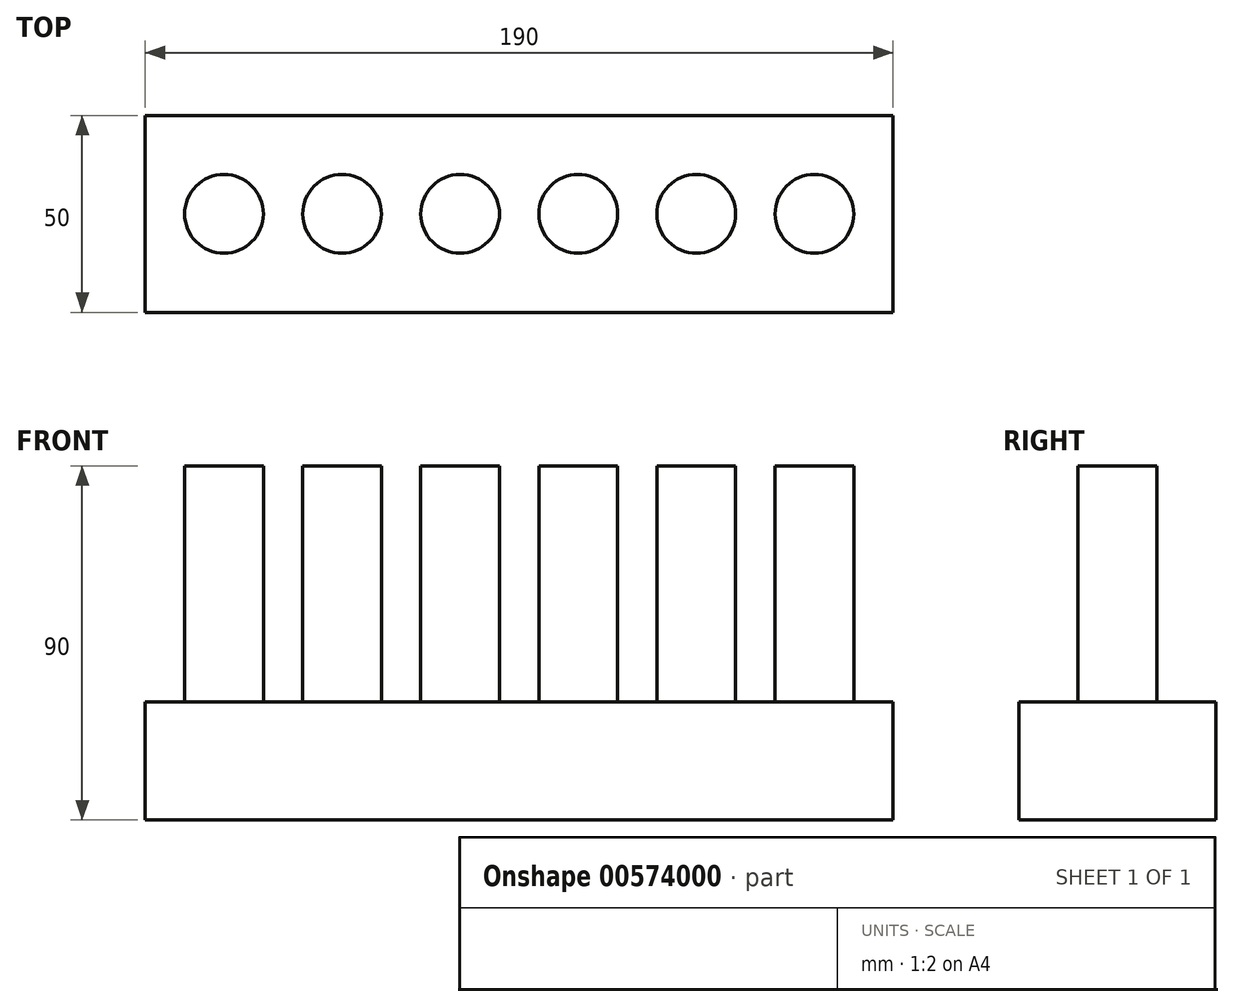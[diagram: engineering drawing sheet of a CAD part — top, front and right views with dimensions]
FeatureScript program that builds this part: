
annotation { "Feature Type Name" : "Feature", "Feature Type Description" : "" }
export const myFeature = defineFeature(function(context is Context, id is Id, definition is map)
    precondition{}
    {
        {
            var Q0;
            Q0=qCreatedBy(makeId("Top.planeOp"),FACE);
            var sketch = newSketch(context, id + "F0", { "sketchPlane" : qUnion([Q0])});
            skLineSegment(sketch, "E0.bottom", {"start": v(0, -25) * mm, "end": v(95, -25) * mm});
            skLineSegment(sketch, "E0.top", {"start": v(0, 25) * mm, "end": v(95, 25) * mm});
            skLineSegment(sketch, "E0.left", {"start": v(0, -25) * mm, "end": v(0, 25) * mm});
            skLineSegment(sketch, "E0.right", {"start": v(95, -25) * mm, "end": v(95, 25) * mm});
            skSolve(sketch);
        }
        {
            var Q0;
            Q0 = qSketchRegion(id + "F0", true);
            extrude(context, id + "F1", {"entities" : qUnion([Q0]), "depth" : 30 * mm, "offsetDistance" : 25 * mm});
        }
        {
            var Q0;
            Q0=makeQuery(id+"F1.opExtrude","CAP_FACE",FACE,{"disambiguationData":[OSD([sQuery(id+"F0.wireOp",EDGE,"E0.bottom"),sQuery(id+"F0.wireOp",EDGE,"E0.top"),sQuery(id+"F0.wireOp",EDGE,"E0.left"),sQuery(id+"F0.wireOp",EDGE,"E0.right")])],"isStart":false});
            var sketch = newSketch(context, id + "F2", { "sketchPlane" : qUnion([Q0])});
            skCircle(sketch, "E1", {"center": v(75, 0) * mm, "radius": 10 * mm});
            skCircle(sketch, "E2", {"center": v(15, 0) * mm, "radius": 10 * mm});
            skCircle(sketch, "E3", {"center": v(45, 0) * mm, "radius": 10 * mm});
            skSolve(sketch);
        }
        {
            var Q0;
            Q0 = qSketchRegion(id + "F2", true);
            extrude(context, id + "F3", {"entities" : qUnion([Q0]), "operationType" : NewBodyOperationType.REMOVE, "oppositeDirection" : true, "depth" : 10 * mm, "offsetDistance" : 25 * mm});
        }
        {
            var Q0;
            Q0=makeQuery(id+"F3.boolean.opBoolean","COPY",FACE,{"derivedFrom":makeQuery(id+"F3.opExtrude","CAP_FACE",FACE,{"disambiguationData":[OSD([sQuery(id+"F2.wireOp",EDGE,"E1")])],"isStart":false})});
            var sketch = newSketch(context, id + "F4", { "sketchPlane" : qUnion([Q0])});
            skCircle(sketch, "E4", {"center": v(75, 0) * mm, "radius": 10 * mm});
            skSolve(sketch);
        }
        {
            var Q0;
            Q0 = qSketchRegion(id + "F4", true);
            extrude(context, id + "F5", {"entities" : qUnion([Q0]), "operationType" : NewBodyOperationType.ADD, "depth" : 70 * mm, "offsetDistance" : 25 * mm});
        }
        {
            var Q0;
            Q0=makeQuery(id+"F3.boolean.opBoolean","COPY",FACE,{"derivedFrom":makeQuery(id+"F3.opExtrude","CAP_FACE",FACE,{"disambiguationData":[OSD([sQuery(id+"F2.wireOp",EDGE,"E3")])],"isStart":false})});
            var sketch = newSketch(context, id + "F6", { "sketchPlane" : qUnion([Q0])});
            skCircle(sketch, "E5", {"center": v(45, 0) * mm, "radius": 10 * mm});
            skSolve(sketch);
        }
        {
            var Q0;
            Q0 = qSketchRegion(id + "F6", true);
            extrude(context, id + "F7", {"entities" : qUnion([Q0]), "operationType" : NewBodyOperationType.ADD, "depth" : 70 * mm, "offsetDistance" : 25 * mm});
        }
        {
            var Q0;
            Q0=makeQuery(id+"F3.boolean.opBoolean","COPY",FACE,{"derivedFrom":makeQuery(id+"F3.opExtrude","CAP_FACE",FACE,{"disambiguationData":[OSD([sQuery(id+"F2.wireOp",EDGE,"E2")])],"isStart":false})});
            var sketch = newSketch(context, id + "F8", { "sketchPlane" : qUnion([Q0])});
            skCircle(sketch, "E6", {"center": v(15, 0) * mm, "radius": 10 * mm});
            skSolve(sketch);
        }
        {
            var Q0;
            Q0 = qSketchRegion(id + "F8", true);
            extrude(context, id + "F9", {"entities" : qUnion([Q0]), "operationType" : NewBodyOperationType.ADD, "depth" : 70 * mm, "offsetDistance" : 25 * mm});
        }
        {
            var Q0;
            Q0=makeQuery(id+"F1.opExtrude","SWEPT_BODY",BODY,{"disambiguationData":[OSD([sQuery(id+"F0.wireOp",EDGE,"E0.bottom"),sQuery(id+"F0.wireOp",EDGE,"E0.top"),sQuery(id+"F0.wireOp",EDGE,"E0.left"),sQuery(id+"F0.wireOp",EDGE,"E0.right")])]});
            var Q1;
            Q1=makeQuery(id+"F1.opExtrude","SWEPT_FACE",FACE,{"disambiguationData":[OSD([sQuery(id+"F0.wireOp",EDGE,"E0.left")])]});
            mirror(context, id + "F10", {"operationType" : NewBodyOperationType.ADD, "entities" : qUnion([Q0]), "mirrorPlane" : qUnion([Q1])});
        }
        {
            var Q0;
            Q0=makeQuery(id+"F1.opExtrude","SWEPT_BODY",BODY,{"disambiguationData":[OSD([sQuery(id+"F0.wireOp",EDGE,"E0.bottom"),sQuery(id+"F0.wireOp",EDGE,"E0.top"),sQuery(id+"F0.wireOp",EDGE,"E0.left"),sQuery(id+"F0.wireOp",EDGE,"E0.right")])]});
            transform(context, id + "F11", {"entities" : qUnion([Q0]), "transformType" : TransformType.TRANSLATION_3D, "dx" : 0 * mm, "dy" : 0 * mm, "dz" : 0 * mm, "makeCopy" : true});
        }
    });
